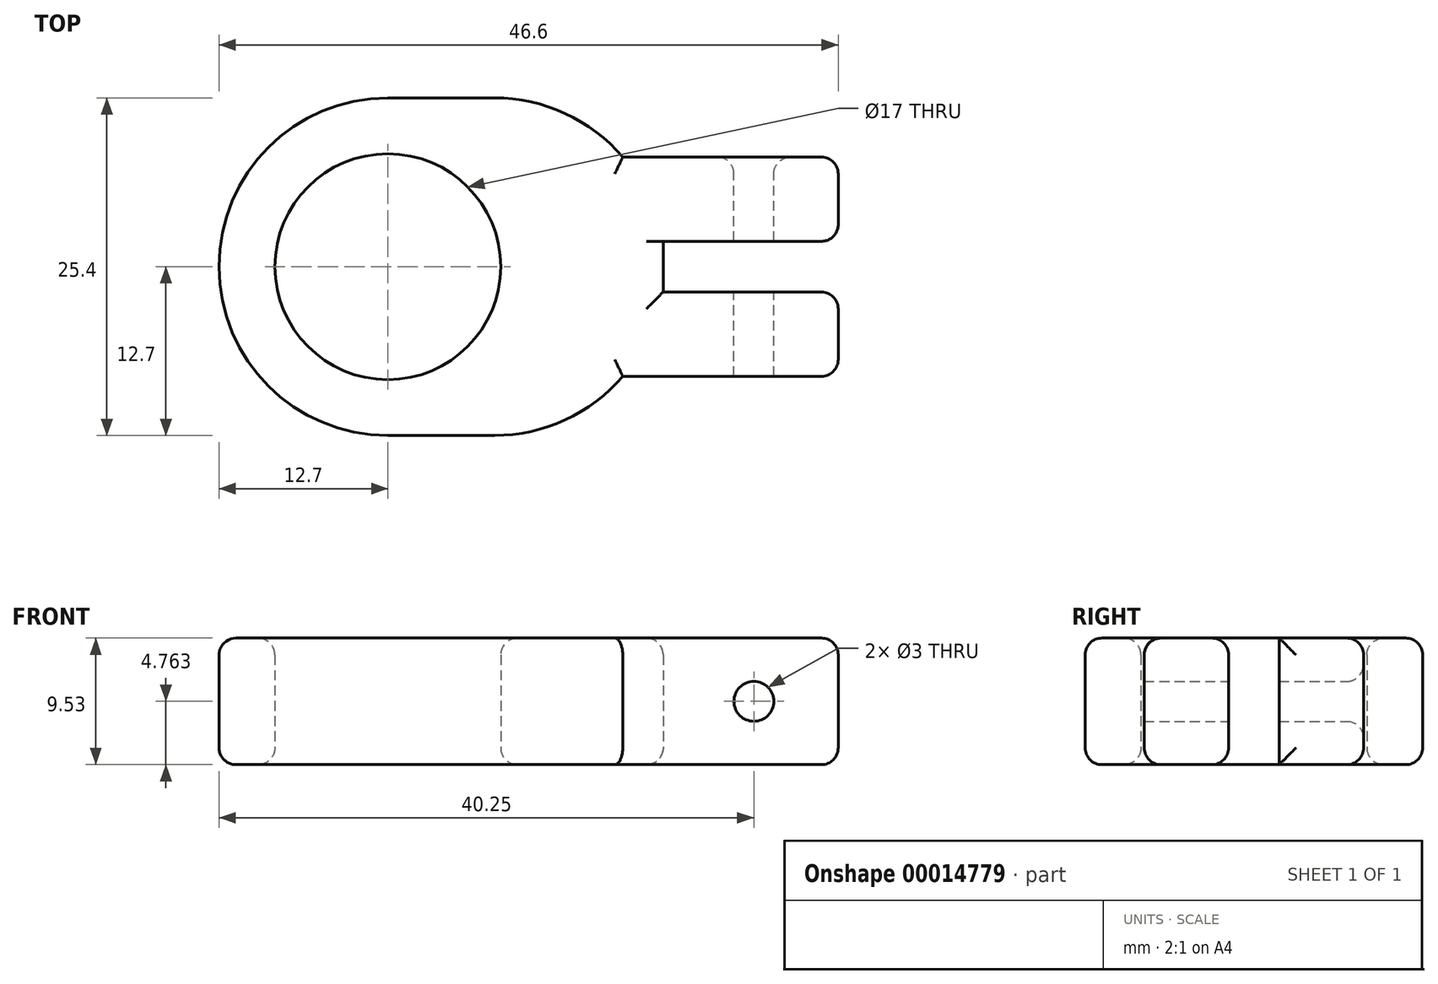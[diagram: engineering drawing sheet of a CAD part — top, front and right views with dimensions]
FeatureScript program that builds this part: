
annotation { "Feature Type Name" : "Feature", "Feature Type Description" : "" }
export const myFeature = defineFeature(function(context is Context, id is Id, definition is map)
    precondition{}
    {
        {
            var Q0;
            Q0=qCreatedBy(makeId("Top.planeOp"),FACE);
            var sketch = newSketch(context, id + "F0", { "sketchPlane" : qUnion([Q0])});
            skLineSegment(sketch, "E0.bottom", {"start": v(12.7, 0) * mm, "end": v(20.73, 0) * mm});
            skLineSegment(sketch, "E0.top", {"start": v(12.7, -25.4) * mm, "end": v(20.73, -25.4) * mm});
            skLineSegment(sketch, "E0.right", {"start": v(33.43, -10.8) * mm, "end": v(33.43, -14.6) * mm});
            skCircle(sketch, "E1", {"center": v(12.7, -12.7) * mm, "radius": 12.7 * mm});
            skLineSegment(sketch, "E2", {"start": v(0, -12.7) * mm, "end": v(33.43, -12.7) * mm});
            skCircle(sketch, "E3", {"center": v(12.7, -12.7) * mm, "radius": 8.5 * mm});
            skCircle(sketch, "E4", {"center": v(20.73, -12.7) * mm, "radius": 12.7 * mm});
            skLineSegment(sketch, "E5.bottom", {"start": v(33.43, -10.8) * mm, "end": v(46.6, -10.8) * mm});
            skLineSegment(sketch, "E5.top", {"start": v(33.43, -14.6) * mm, "end": v(46.6, -14.6) * mm});
            skLineSegment(sketch, "E6", {"start": v(33.43, -14.6) * mm, "end": v(33.28, -14.6) * mm});
            skPoint(sketch, "E7.orphan", {"position": v(33.43, -25.4) * mm});
            skPoint(sketch, "E8.orphan", {"position": v(33.43, 0) * mm});
            skLineSegment(sketch, "E9.bottom", {"start": v(46.6, -10.8) * mm, "end": v(33.43, -10.8) * mm});
            skLineSegment(sketch, "E9.top", {"start": v(46.6, -4.44) * mm, "end": v(33.43, -4.45) * mm});
            skLineSegment(sketch, "E9.left", {"start": v(46.6, -10.8) * mm, "end": v(46.6, -4.44) * mm});
            skLineSegment(sketch, "E9.right", {"start": v(33.43, -10.8) * mm, "end": v(33.43, -4.45) * mm});
            skLineSegment(sketch, "E10.top", {"start": v(33.43, -20.96) * mm, "end": v(46.6, -20.96) * mm});
            skLineSegment(sketch, "E10.left", {"start": v(33.43, -14.6) * mm, "end": v(33.43, -20.96) * mm});
            skLineSegment(sketch, "E10.right", {"start": v(46.6, -14.6) * mm, "end": v(46.6, -20.96) * mm});
            skLineSegment(sketch, "E11", {"start": v(33.43, -4.45) * mm, "end": v(30.38, -4.45) * mm});
            skLineSegment(sketch, "E12", {"start": v(33.43, -20.96) * mm, "end": v(30.38, -20.96) * mm});
            skSolve(sketch);
        }
        {
            var Q0;
            Q0 = qSketchRegion(id + "F0", true);
            var Q1;
            {var subQ0=sQuery(id+"F0.wireOp",EDGE,"E4");var subQ3=sQuery(id+"F0.wireOp",EDGE,"E1");var subQ4=makeQuery(id+"F0.imprint","INTERSECT",VERTEX,{"disambiguationData":[OD(0.0)],"derivedFrom":[subQ3,subQ0]});Q1=makeQuery(id+"F0.imprint","IMPRINT",FACE,{"disambiguationData":[TD([[makeQuery(id+"F0.imprint","IMPRINT",EDGE,{"disambiguationData":[TD([[subQ4,1.0]])],"derivedFrom":subQ3}),1.0]])]});}
            var Q2;
            {var subQ3=sQuery(id+"F0.wireOp",EDGE,"E1");var subQ5=sQuery(id+"F0.wireOp",EDGE,"E2");var subQ7=makeQuery(id+"F0.imprint","INTERSECT",VERTEX,{"disambiguationData":[OD(1.0)],"derivedFrom":[subQ3,subQ5]});Q2=makeQuery(id+"F0.imprint","IMPRINT",FACE,{"disambiguationData":[TD([[makeQuery(id+"F0.imprint","IMPRINT",EDGE,{"disambiguationData":[TD([[subQ7,1.0]])],"derivedFrom":subQ3}),1.0]])]});}
            extrude(context, id + "F1", {"entities" : qUnion([Q0, Q1, Q2]), "depth" : 9.52 * mm});
        }
        {
            var Q0;
            Q0=qCreatedBy(makeId("Front.planeOp"),FACE);
            var sketch = newSketch(context, id + "F2", { "sketchPlane" : qUnion([Q0])});
            skLineSegment(sketch, "E13.0.0", {"start": v(30.38, 0) * mm, "end": v(46.6, 0) * mm});
            skLineSegment(sketch, "E13.0.1", {"start": v(46.6, 0) * mm, "end": v(46.6, 9.53) * mm});
            skLineSegment(sketch, "E13.0.2", {"start": v(46.6, 9.53) * mm, "end": v(30.38, 9.53) * mm});
            skLineSegment(sketch, "E13.0.3", {"start": v(30.38, 9.53) * mm, "end": v(30.38, 0) * mm});
            skCircle(sketch, "E14", {"center": v(40.25, 4.76) * mm, "radius": 1.5 * mm});
            skSolve(sketch);
        }
        {
            var Q0;
            Q0=makeQuery(id+"F2.imprint","IMPRINT",FACE,{"disambiguationData":[TD([[makeQuery(id+"F2.imprint","IMPRINT",EDGE,{"derivedFrom":sQuery(id+"F2.wireOp",EDGE,"E14")}),1.0]])]});
            extrude(context, id + "F3", {"entities" : qUnion([Q0]), "operationType" : NewBodyOperationType.REMOVE, "endBound" : BoundingType.THROUGH_ALL, "depth" : 25.4 * mm});
        }
        {
            var Q0;
            Q0=makeQuery(id+"F1.opExtrude","CAP_EDGE",EDGE,{"disambiguationData":[OSD([sQuery(id+"F0.wireOp",EDGE,"E3")])],"isStart":false});
            var Q1;
            Q1=makeQuery(id+"F1.opExtrude","CAP_EDGE",EDGE,{"disambiguationData":[OSD([sQuery(id+"F0.wireOp",EDGE,"E1")])],"isStart":false});
            var Q2;
            Q2=makeQuery(id+"F1.opExtrude","CAP_EDGE",EDGE,{"disambiguationData":[OSD([sQuery(id+"F0.wireOp",EDGE,"E0.top")])],"isStart":false});
            var Q3;
            Q3=makeQuery(id+"F1.opExtrude","CAP_EDGE",EDGE,{"disambiguationData":[OSD([sQuery(id+"F0.wireOp",EDGE,"E10.top"),sQuery(id+"F0.wireOp",EDGE,"E12")])],"isStart":false});
            var Q4;
            Q4=makeQuery(id+"F1.opExtrude","CAP_EDGE",EDGE,{"disambiguationData":[OSD([sQuery(id+"F0.wireOp",EDGE,"E9.bottom")])],"isStart":false});
            var Q5;
            Q5=makeQuery(id+"F1.opExtrude","CAP_EDGE",EDGE,{"disambiguationData":[OSD([sQuery(id+"F0.wireOp",EDGE,"E5.top")])],"isStart":false});
            var Q6;
            Q6=makeQuery(id+"F1.opExtrude","CAP_EDGE",EDGE,{"disambiguationData":[OSD([sQuery(id+"F0.wireOp",EDGE,"E0.right")])],"isStart":false});
            var Q7;
            Q7=makeQuery(id+"F1.opExtrude","CAP_EDGE",EDGE,{"disambiguationData":[OSD([sQuery(id+"F0.wireOp",EDGE,"E9.top"),sQuery(id+"F0.wireOp",EDGE,"E11")])],"isStart":false});
            var Q8;
            Q8=makeQuery(id+"F1.opExtrude","SWEPT_EDGE",EDGE,{"disambiguationData":[OSD([sQuery(id+"F0.wireOp",EDGE,"E9.bottom"),sQuery(id+"F0.wireOp",EDGE,"E9.left")])]});
            var Q9;
            Q9=makeQuery(id+"F1.opExtrude","CAP_EDGE",EDGE,{"disambiguationData":[OSD([sQuery(id+"F0.wireOp",EDGE,"E10.right")])],"isStart":false});
            var Q10;
            Q10=makeQuery(id+"F1.opExtrude","CAP_EDGE",EDGE,{"disambiguationData":[OSD([sQuery(id+"F0.wireOp",EDGE,"E9.left")])],"isStart":false});
            var Q11;
            Q11=makeQuery(id+"F1.opExtrude","CAP_EDGE",EDGE,{"disambiguationData":[OSD([sQuery(id+"F0.wireOp",EDGE,"E10.right")])],"isStart":true});
            var Q12;
            Q12=makeQuery(id+"F1.opExtrude","SWEPT_EDGE",EDGE,{"disambiguationData":[OSD([sQuery(id+"F0.wireOp",EDGE,"E10.top"),sQuery(id+"F0.wireOp",EDGE,"E10.right")])]});
            var Q13;
            Q13=makeQuery(id+"F1.opExtrude","SWEPT_EDGE",EDGE,{"disambiguationData":[OSD([sQuery(id+"F0.wireOp",EDGE,"E9.top"),sQuery(id+"F0.wireOp",EDGE,"E9.left")])]});
            var Q14;
            Q14=makeQuery(id+"F1.opExtrude","CAP_EDGE",EDGE,{"disambiguationData":[OSD([sQuery(id+"F0.wireOp",EDGE,"E9.left")])],"isStart":true});
            var Q15;
            {var subQ0=sQuery(id+"F0.wireOp",EDGE,"E4");Q15=makeQuery(id+"F1.opExtrude","CAP_EDGE",EDGE,{"disambiguationData":[OSD([subQ0]),TDD([makeQuery(id+"F0.imprint","IMPRINT",EDGE,{"disambiguationData":[TD([[makeQuery(id+"F0.imprint","INTERSECT",VERTEX,{"derivedFrom":[sQuery(id+"F0.wireOp",EDGE,"E0.top"),subQ0]}),-1.0]])],"derivedFrom":subQ0})])],"isStart":true});}
            var Q16;
            Q16=makeQuery(id+"F1.opExtrude","CAP_EDGE",EDGE,{"disambiguationData":[OSD([sQuery(id+"F0.wireOp",EDGE,"E10.top"),sQuery(id+"F0.wireOp",EDGE,"E12")])],"isStart":true});
            var Q17;
            Q17=makeQuery(id+"F1.opExtrude","SWEPT_EDGE",EDGE,{"disambiguationData":[OSD([sQuery(id+"F0.wireOp",EDGE,"E5.top"),sQuery(id+"F0.wireOp",EDGE,"E10.right")])]});
            var Q18;
            Q18=makeQuery(id+"F1.opExtrude","CAP_EDGE",EDGE,{"disambiguationData":[OSD([sQuery(id+"F0.wireOp",EDGE,"E5.top")])],"isStart":true});
            var Q19;
            Q19=makeQuery(id+"F1.opExtrude","CAP_EDGE",EDGE,{"disambiguationData":[OSD([sQuery(id+"F0.wireOp",EDGE,"E9.bottom")])],"isStart":true});
            var Q20;
            Q20=makeQuery(id+"F1.opExtrude","CAP_EDGE",EDGE,{"disambiguationData":[OSD([sQuery(id+"F0.wireOp",EDGE,"E0.right")])],"isStart":true});
            var Q21;
            Q21=makeQuery(id+"F1.opExtrude","CAP_EDGE",EDGE,{"disambiguationData":[OSD([sQuery(id+"F0.wireOp",EDGE,"E9.top"),sQuery(id+"F0.wireOp",EDGE,"E11")])],"isStart":true});
            var Q22;
            Q22=makeQuery(id+"F1.opExtrude","CAP_EDGE",EDGE,{"disambiguationData":[OSD([sQuery(id+"F0.wireOp",EDGE,"E3")])],"isStart":true});
            var Q23;
            Q23=makeQuery(id+"F3.boolean.opBoolean","INTERSECT",EDGE,{"derivedFrom":[makeQuery(id+"F1.opExtrude","SWEPT_FACE",FACE,{"disambiguationData":[OSD([sQuery(id+"F0.wireOp",EDGE,"E9.top"),sQuery(id+"F0.wireOp",EDGE,"E11")])]}),makeQuery(id+"F3.opExtrude","SWEPT_FACE",FACE,{"disambiguationData":[OSD([sQuery(id+"F2.wireOp",EDGE,"E14")])]})]});
            fillet(context, id + "F4", {"entities" : qUnion([Q0, Q1, Q2, Q3, Q4, Q5, Q6, Q7, Q8, Q9, Q10, Q11, Q12, Q13, Q14, Q15, Q16, Q17, Q18, Q19, Q20, Q21, Q22, Q23]), "radius" : 1.27 * mm, "tangentPropagation" : true, "allowEdgeOverflow" : false});
        }
    });
